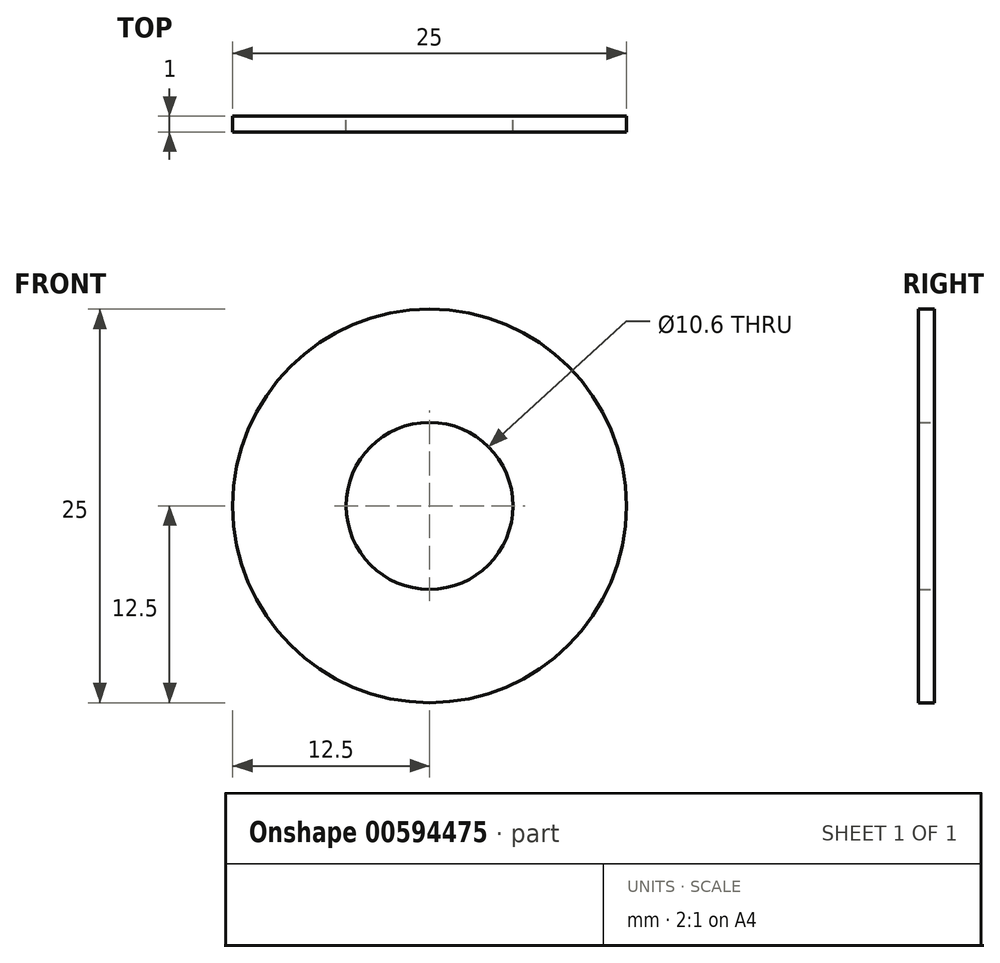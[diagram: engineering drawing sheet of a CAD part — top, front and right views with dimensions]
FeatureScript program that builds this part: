
annotation { "Feature Type Name" : "Feature", "Feature Type Description" : "" }
export const myFeature = defineFeature(function(context is Context, id is Id, definition is map)
    precondition{}
    {
        {
            var Q0;
            Q0=qCreatedBy(makeId("Front.planeOp"),FACE);
            var sketch = newSketch(context, id + "F0", { "sketchPlane" : qUnion([Q0])});
            skCircle(sketch, "E0", {"center": v(0, 0) * mm, "radius": 12.5 * mm});
            skCircle(sketch, "E1", {"center": v(0, 0) * mm, "radius": 5.3 * mm});
            skSolve(sketch);
        }
        {
            var Q0;
            Q0=qSketchRegion(id+"F0",true);
            extrude(context, id + "F1", {"entities" : qUnion([Q0]), "depth" : 1 * mm});
        }
    });
